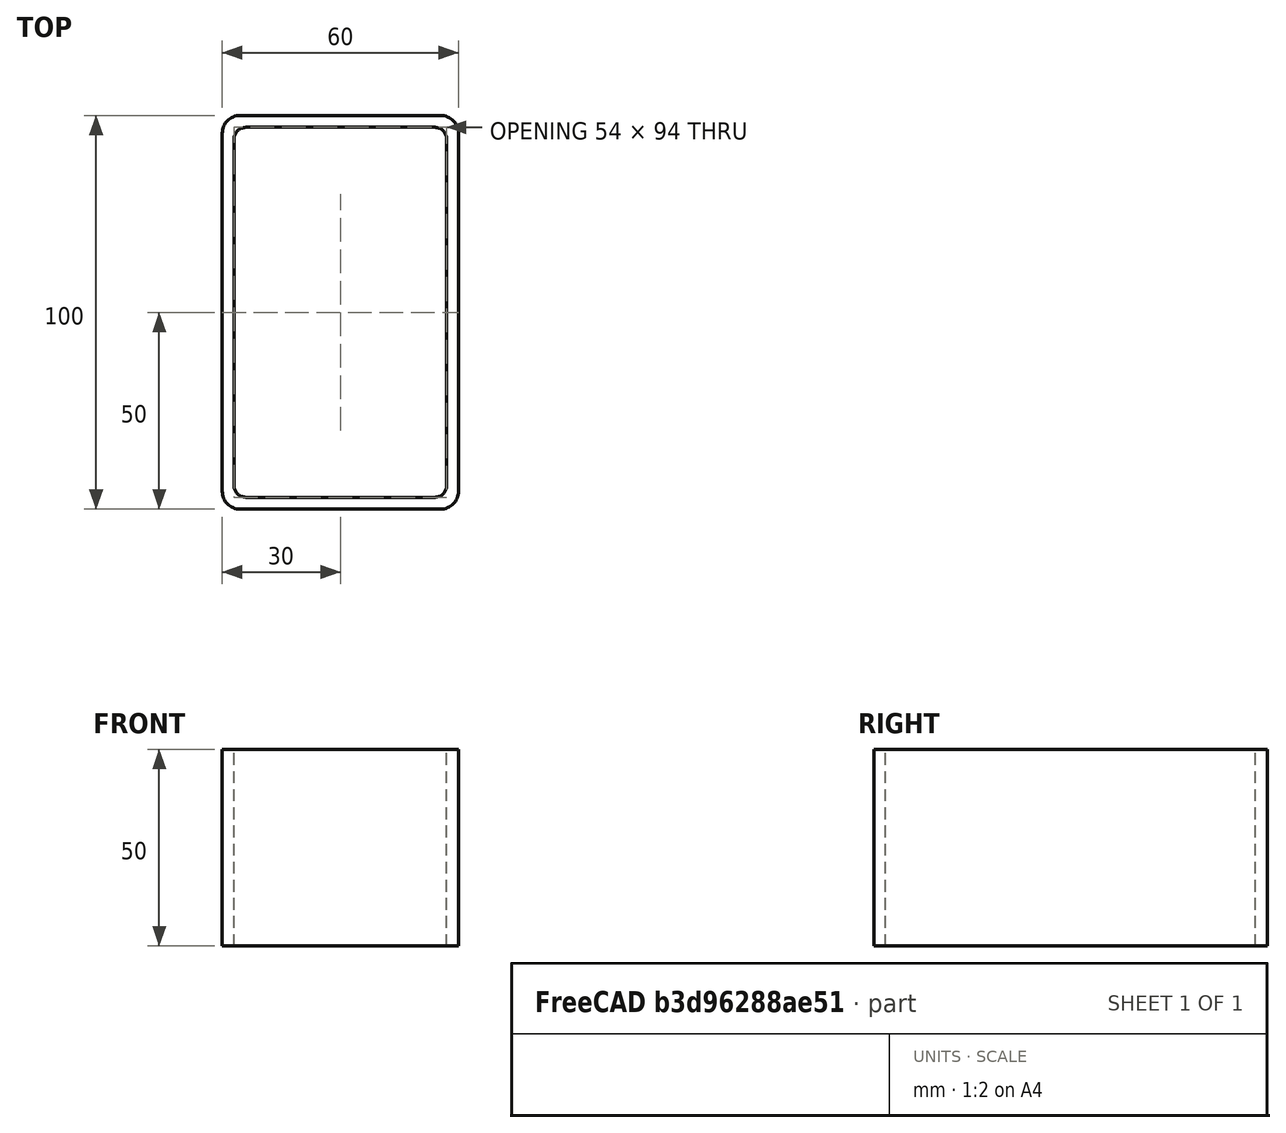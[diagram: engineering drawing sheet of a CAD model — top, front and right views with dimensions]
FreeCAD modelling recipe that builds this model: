
FCSTD DOCUMENT  (FreeCAD 0.15R4671 (Git))
Label: Rectangular hollow section 100x60x3 EN10219 S235JRH
License: All rights reserved
LicenseURL: http://en.wikipedia.org/wiki/All_rights_reserved
objects: Sketcher::SketchObject×1, Part::Extrusion×1
note: 2 computed .brp shape members not serialized (recipe doc carries the construction recipe); baked Part::Feature solids carry a one-line shape summary decoded from their .brp

FEATURE [Sketcher::SketchObject] Sketch
  sketch-geometry (16):
    g0: LineSegment StartX=-24 StartY=47 StartZ=0 EndX=24 EndY=47 EndZ=0
    g1: LineSegment StartX=27 StartY=44 StartZ=0 EndX=27 EndY=-44 EndZ=0
    g2: LineSegment StartX=24 StartY=-47 StartZ=0 EndX=-24 EndY=-47 EndZ=0
    g3: LineSegment StartX=-27 StartY=-44 StartZ=0 EndX=-27 EndY=44 EndZ=0
    g4: LineSegment StartX=-25.5 StartY=50 StartZ=0 EndX=25.5 EndY=50 EndZ=0
    g5: LineSegment StartX=30 StartY=45.5 StartZ=0 EndX=30 EndY=-45.5 EndZ=0
    g6: LineSegment StartX=25.5 StartY=-50 StartZ=0 EndX=-25.5 EndY=-50 EndZ=0
    g7: LineSegment StartX=-30 StartY=-45.5 StartZ=0 EndX=-30 EndY=45.5 EndZ=0
    g8: ArcOfCircle CenterX=-24 CenterY=44 CenterZ=0 NormalX=0 NormalY=0 NormalZ=1 Radius=3 StartAngle=1.5708 EndAngle=3.14159
    g9: ArcOfCircle CenterX=24 CenterY=44 CenterZ=0 NormalX=0 NormalY=0 NormalZ=1 Radius=3 StartAngle=0 EndAngle=1.5708
    g10: ArcOfCircle CenterX=24 CenterY=-44 CenterZ=0 NormalX=0 NormalY=0 NormalZ=1 Radius=3 StartAngle=4.71239 EndAngle=6.28319
    g11: ArcOfCircle CenterX=-24 CenterY=-44 CenterZ=0 NormalX=0 NormalY=0 NormalZ=1 Radius=3 StartAngle=3.14159 EndAngle=4.71239
    g12: ArcOfCircle CenterX=25.5 CenterY=45.5 CenterZ=0 NormalX=0 NormalY=0 NormalZ=1 Radius=4.5 StartAngle=0 EndAngle=1.5708
    g13: ArcOfCircle CenterX=25.5 CenterY=-45.5 CenterZ=0 NormalX=0 NormalY=0 NormalZ=1 Radius=4.5 StartAngle=4.71239 EndAngle=6.28319
    g14: ArcOfCircle CenterX=-25.5 CenterY=-45.5 CenterZ=0 NormalX=0 NormalY=0 NormalZ=1 Radius=4.5 StartAngle=3.14159 EndAngle=4.71239
    g15: ArcOfCircle CenterX=-25.5 CenterY=45.5 CenterZ=0 NormalX=0 NormalY=0 NormalZ=1 Radius=4.5 StartAngle=1.5708 EndAngle=3.14159
  constraints (36):
    c: Horizontal(g2)
    c: Vertical(g3)
    c: Horizontal(g6)
    c: Vertical(g7)
    c: Tangent(g3,g8) = 1.5708
    c: Tangent(g0,g8) = 1.5708
    c: Tangent(g0,g9) = 1.5708
    c: Tangent(g1,g9) = 1.5708
    c: Tangent(g1,g10) = 1.5708
    c: Tangent(g2,g10) = 1.5708
    c: Tangent(g2,g11) = 1.5708
    c: Tangent(g3,g11) = 1.5708
    c: Tangent(g4,g12) = 1.5708
    c: Tangent(g5,g12) = 1.5708
    c: Tangent(g5,g13) = 1.5708
    c: Tangent(g6,g13) = 1.5708
    c: Tangent(g6,g14) = 1.5708
    c: Tangent(g7,g14) = 1.5708
    c: Tangent(g7,g15) = 1.5708
    c: Tangent(g4,g15) = 1.5708
    c: Equal(g9,g8)
    c: Equal(g9,g11)
    c: Equal(g9,g10)
    c: Equal(g12,g15)
    c: Equal(g12,g14)
    c: Equal(g12,g13)
    c: Symmetric(g4,g6,g-1)
    c: Symmetric(g7,g5,g-2)
    c: DistanceY(g4,g6) = -100
    c: DistanceX(g7,g5) = 60
    c: Symmetric(g3,g1,g-2)
    c: Symmetric(g0,g2,g-1)
    c: DistanceY(g0,g4) = 3
    c: DistanceX(g5,g1) = -3
    c: Radius(g9) = 3
    c: Radius(g12) = 4.5
FEATURE [Part::Extrusion] Extrude  label="Rectangular hollow section 100x60x3 EN10219 S235JRH"
  Base = -> Sketch
  Dir = (0,0,50)
  Solid = true
